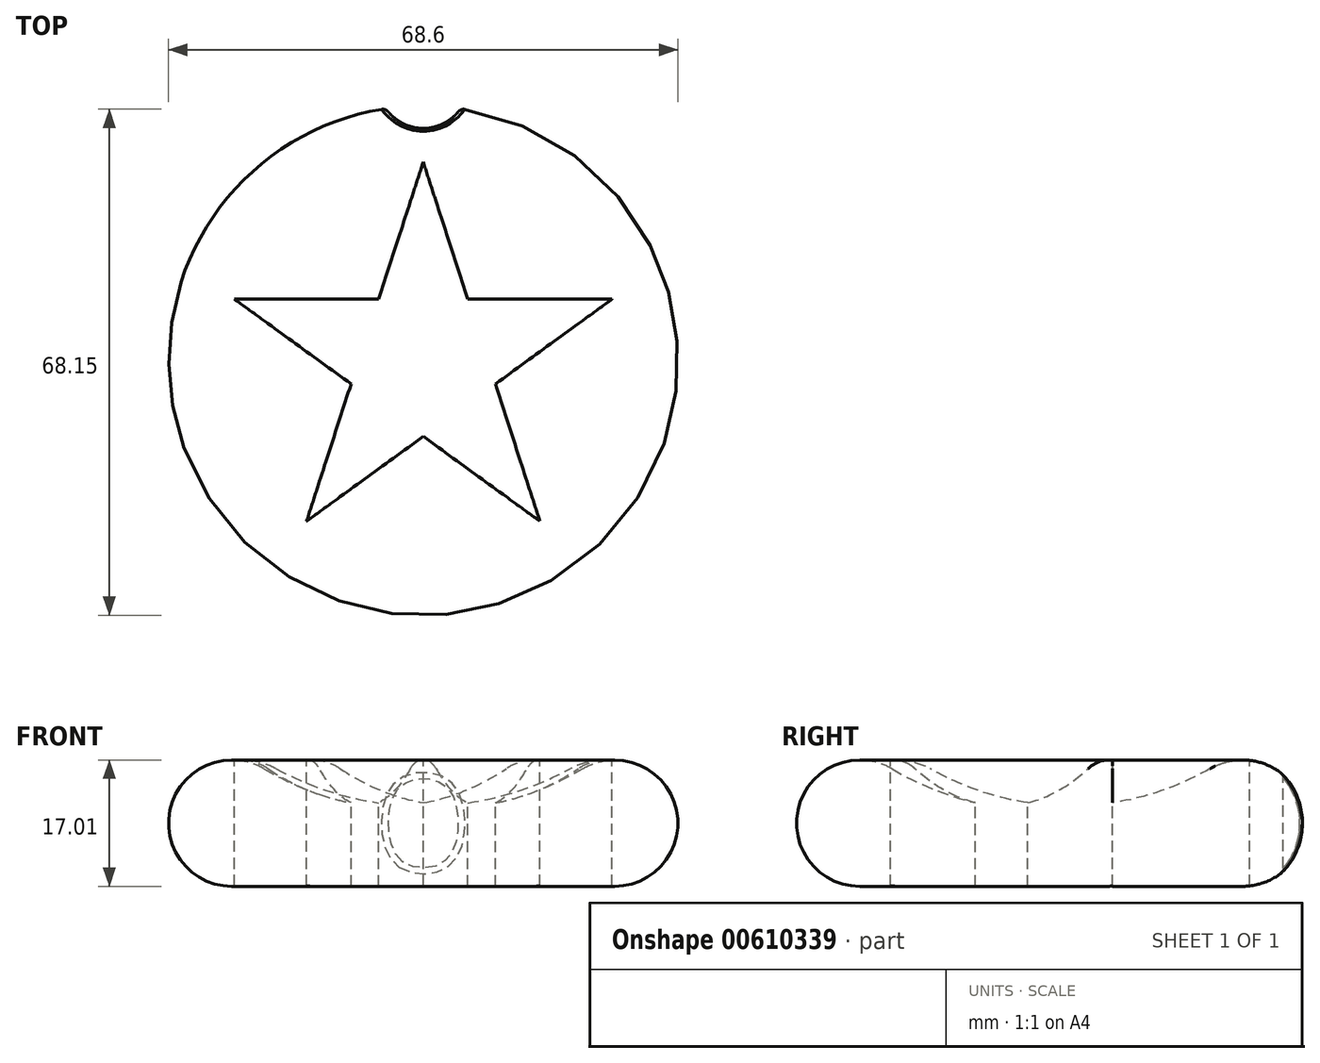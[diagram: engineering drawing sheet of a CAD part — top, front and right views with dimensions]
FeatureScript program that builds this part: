
annotation { "Feature Type Name" : "Feature", "Feature Type Description" : "" }
export const myFeature = defineFeature(function(context is Context, id is Id, definition is map)
    precondition{}
    {
        {
            var Q0;
            Q0=qCreatedBy(makeId("Front.planeOp"),FACE);
            var sketch = newSketch(context, id + "F0", { "sketchPlane" : qUnion([Q0])});
            skArc(sketch, "E0", {"start": v(-21.49, 15.84) * mm, "mid": v(-11.13, 11.49) * mm, "end": v(0, 10) * mm});
            skCircle(sketch, "E1", {"center": v(-25.8, 8.5) * mm, "radius": 8.5 * mm});
            skLineSegment(sketch, "E2", {"start": v(0, 0) * mm, "end": v(0, 10) * mm});
            skLineSegment(sketch, "E3", {"start": v(0, 0) * mm, "end": v(-25.8, 0) * mm});
            skSolve(sketch);
        }
        {
            var Q0;
            {var subQ0=sQuery(id+"F0.wireOp",EDGE,"E0");Q0=makeQuery(id+"F0.imprint","IMPRINT",FACE,{"disambiguationData":[TD([[makeQuery(id+"F0.imprint","IMPRINT",EDGE,{"derivedFrom":subQ0}),-1.0]])]});}
            var Q1;
            {var subQ0=sQuery(id+"F0.wireOp",EDGE,"E1");var subQ1=makeQuery(id+"F0.imprint","INTERSECT",VERTEX,{"derivedFrom":[sQuery(id+"F0.wireOp",EDGE,"E0"),subQ0]});Q1=makeQuery(id+"F0.imprint","IMPRINT",FACE,{"disambiguationData":[TD([[makeQuery(id+"F0.imprint","IMPRINT",EDGE,{"disambiguationData":[TD([[subQ1,-1.0]])],"derivedFrom":subQ0}),1.0]])]});}
            var Q2;
            Q2=sQuery(id+"F0.wireOp",EDGE,"E2");
            revolve(context, id + "F1", {"entities" : qUnion([Q0, Q1]), "axis" : qUnion([Q2]), "revolveType" : RevolveType.FULL});
        }
        {
            var Q0;
            Q0=qCreatedBy(makeId("Top.planeOp"),FACE);
            cPlane(context, id + "F2", {"entities" : qUnion([Q0]), "cplaneType" : CPlaneType.OFFSET, "offset" : 18 * mm, "width" : 150 * mm, "height" : 150 * mm});
        }
        {
            var Q0;
            Q0=qCreatedBy(id+"F2.planeOp",FACE);
            var sketch = newSketch(context, id + "F3", { "sketchPlane" : qUnion([Q0])});
            skLineSegment(sketch, "E4", {"start": v(0, 26.74) * mm, "end": v(-15.72, -21.64) * mm});
            skLineSegment(sketch, "E5", {"start": v(0, 26.74) * mm, "end": v(15.72, -21.64) * mm});
            skLineSegment(sketch, "E6", {"start": v(-25.44, 8.26) * mm, "end": v(25.44, 8.26) * mm});
            skLineSegment(sketch, "E7", {"start": v(-25.44, 8.26) * mm, "end": v(15.72, -21.64) * mm});
            skLineSegment(sketch, "E8", {"start": v(-15.72, -21.64) * mm, "end": v(25.44, 8.26) * mm});
            skSolve(sketch);
        }
        {
            var Q0;
            Q0 = qSketchRegion(id + "F3", true);
            extrude(context, id + "F4", {"entities" : qUnion([Q0]), "operationType" : NewBodyOperationType.REMOVE, "oppositeDirection" : true, "depth" : 25 * mm, "offsetDistance" : 25 * mm});
        }
        {
            var Q0;
            Q0=qCreatedBy(makeId("Front.planeOp"),FACE);
            var sketch = newSketch(context, id + "F5", { "sketchPlane" : qUnion([Q0])});
            skCircle(sketch, "E9", {"center": v(-25.8, 8.5) * mm, "radius": 6.83 * mm});
            skSolve(sketch);
        }
        {
            var Q0;
            Q0=sQuery(id+"F5.wireOp",EDGE,"E9");
            var Q1;
            Q1=sQuery(id+"F0.wireOp",EDGE,"E2");
            revolve(context, id + "F6", {"bodyType" : ToolBodyType.SURFACE, "surfaceEntities" : qUnion([Q0]), "axis" : qUnion([Q1]), "revolveType" : RevolveType.FULL});
        }
        {
            var Q0;
            Q0=qCreatedBy(id+"F2.planeOp",FACE);
            var sketch = newSketch(context, id + "F7", { "sketchPlane" : qUnion([Q0])});
            skCircle(sketch, "E10", {"center": v(0, 37.32) * mm, "radius": 6.06 * mm});
            skSolve(sketch);
        }
        {
            var Q0;
            Q0 = qSketchRegion(id + "F7", true);
            extrude(context, id + "F8", {"entities" : qUnion([Q0]), "operationType" : NewBodyOperationType.REMOVE, "oppositeDirection" : true, "depth" : 25 * mm, "offsetDistance" : 25 * mm});
        }
        {
            var Q0;
            Q0=makeQuery(id+"F8.boolean.opBoolean","INTERSECT",EDGE,{"derivedFrom":[makeQuery(id+"F1.opRevolve","SWEPT_FACE",FACE,{"disambiguationData":[OSD([sQuery(id+"F0.wireOp",EDGE,"E1")])]}),makeQuery(id+"F8.opExtrude","SWEPT_FACE",FACE,{"disambiguationData":[OSD([sQuery(id+"F7.wireOp",EDGE,"E10")])]})]});
            fillet(context, id + "F9", {"entities" : qUnion([Q0]), "radius" : 1 * mm, "tangentPropagation" : true, "allowEdgeOverflow" : false});
        }
    });
